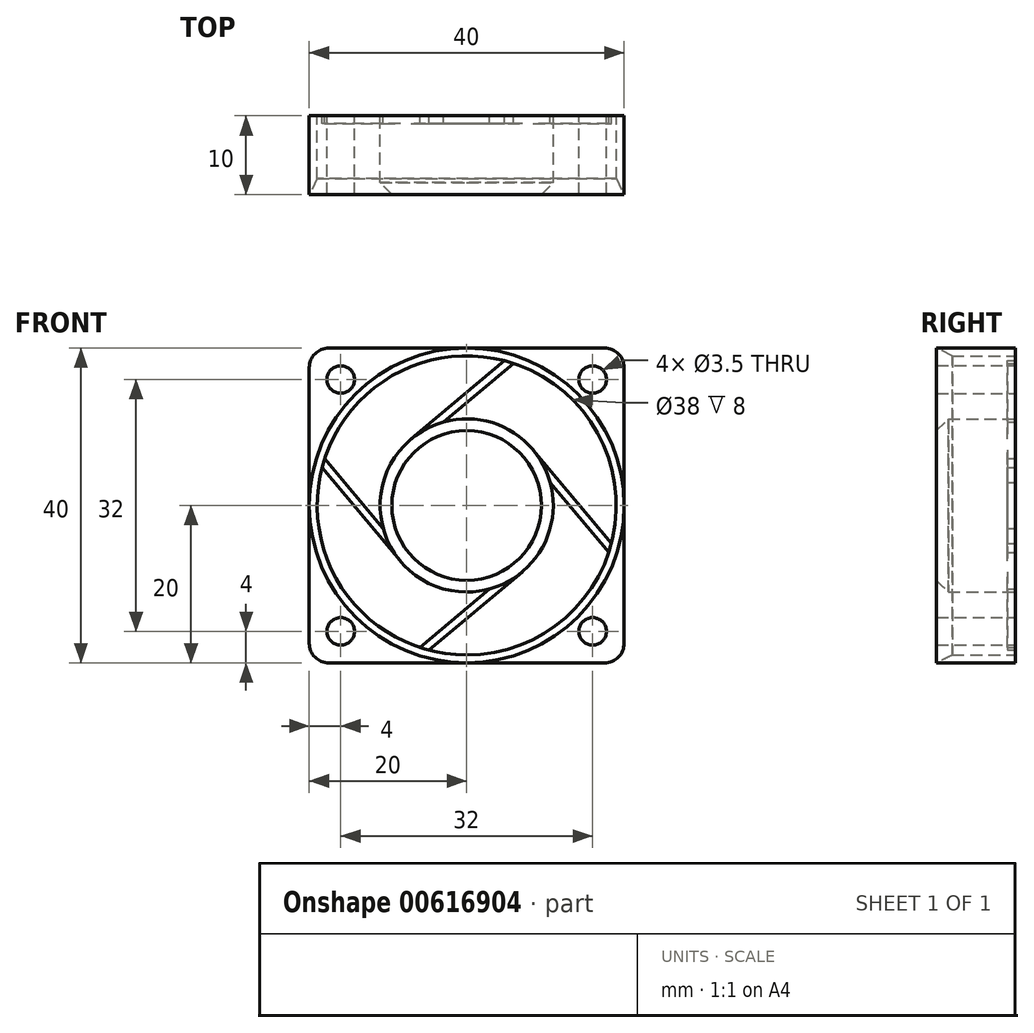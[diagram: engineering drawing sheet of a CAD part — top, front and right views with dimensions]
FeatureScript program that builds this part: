
annotation { "Feature Type Name" : "Feature", "Feature Type Description" : "" }
export const myFeature = defineFeature(function(context is Context, id is Id, definition is map)
    precondition{}
    {
        {
            var Q0;
            Q0=qCreatedBy(makeId("Front.planeOp"),FACE);
            var sketch = newSketch(context, id + "F0", { "sketchPlane" : qUnion([Q0])});
            skLineSegment(sketch, "E0.bottom", {"start": v(17.5, -20) * mm, "end": v(-17.5, -20) * mm});
            skLineSegment(sketch, "E0.top", {"start": v(17.5, 20) * mm, "end": v(-17.5, 20) * mm});
            skLineSegment(sketch, "E0.left", {"start": v(20, -17.5) * mm, "end": v(20, 17.5) * mm});
            skLineSegment(sketch, "E0.right", {"start": v(-20, -17.5) * mm, "end": v(-20, 17.5) * mm});
            skPoint(sketch, "E0.middle", {"position": v(0, 0) * mm});
            skLineSegment(sketch, "E1.bottom", {"start": v(16, 16) * mm, "end": v(-16, 16) * mm, "construction": true});
            skLineSegment(sketch, "E1.top", {"start": v(16, -16) * mm, "end": v(-16, -16) * mm, "construction": true});
            skLineSegment(sketch, "E1.left", {"start": v(16, 16) * mm, "end": v(16, -16) * mm, "construction": true});
            skLineSegment(sketch, "E1.right", {"start": v(-16, 16) * mm, "end": v(-16, -16) * mm, "construction": true});
            skCircle(sketch, "E2", {"center": v(16, 16) * mm, "radius": 1.75 * mm});
            skCircle(sketch, "E3", {"center": v(-16, 16) * mm, "radius": 1.75 * mm});
            skCircle(sketch, "E4", {"center": v(-16, -16) * mm, "radius": 1.75 * mm});
            skCircle(sketch, "E5", {"center": v(16, -16) * mm, "radius": 1.75 * mm});
            skCircle(sketch, "E6", {"center": v(0, 0) * mm, "radius": 19 * mm});
            skPoint(sketch, "E7.visualSharp", {"position": v(20, 20) * mm});
            skArc(sketch, "E7.filletArc", {"start": v(20, 17.5) * mm, "mid": v(19.27, 19.27) * mm, "end": v(17.5, 20) * mm});
            skPoint(sketch, "E8.visualSharp", {"position": v(20, -20) * mm});
            skArc(sketch, "E8.filletArc", {"start": v(17.5, -20) * mm, "mid": v(19.27, -19.27) * mm, "end": v(20, -17.5) * mm});
            skPoint(sketch, "E9.visualSharp", {"position": v(-20, -20) * mm});
            skArc(sketch, "E9.filletArc", {"start": v(-20, -17.5) * mm, "mid": v(-19.27, -19.27) * mm, "end": v(-17.5, -20) * mm});
            skPoint(sketch, "E10.visualSharp", {"position": v(-20, 20) * mm});
            skArc(sketch, "E10.filletArc", {"start": v(-17.5, 20) * mm, "mid": v(-19.27, 19.27) * mm, "end": v(-20, 17.5) * mm});
            skSolve(sketch);
        }
        {
            var Q0;
            Q0 = qSketchRegion(id + "F0", true);
            extrude(context, id + "F1", {"entities" : qUnion([Q0]), "depth" : 10 * mm, "offsetDistance" : 25 * mm});
        }
        {
            var Q0;
            Q0=qCreatedBy(makeId("Front.planeOp"),FACE);
            var sketch = newSketch(context, id + "F2", { "sketchPlane" : qUnion([Q0])});
            skArc(sketch, "E11", {"start": v(-7.07, 8.43) * mm, "mid": v(-10.5, 3.27) * mm, "end": v(-10.6, -2.92) * mm});
            skLineSegment(sketch, "E12", {"start": v(-7.07, 8.43) * mm, "end": v(5.63, 19.09) * mm});
            skLineSegment(sketch, "E13", {"start": v(5.63, 19.09) * mm, "end": v(6.28, 18.32) * mm});
            skLineSegment(sketch, "E14", {"start": v(6.28, 18.32) * mm, "end": v(-2.92, 10.6) * mm});
            skLineSegment(sketch, "E15", {"start": v(0, 0) * mm, "end": v(0, 20) * mm, "construction": true});
            skLineSegment(sketch, "E16.1.0", {"start": v(-18.32, 6.28) * mm, "end": v(-10.6, -2.92) * mm});
            skLineSegment(sketch, "E16.1.1", {"start": v(-8.43, -7.07) * mm, "end": v(-19.09, 5.63) * mm});
            skLineSegment(sketch, "E16.1.2", {"start": v(-19.09, 5.63) * mm, "end": v(-18.32, 6.28) * mm});
            skLineSegment(sketch, "E16.2.0", {"start": v(-6.28, -18.32) * mm, "end": v(2.92, -10.6) * mm});
            skLineSegment(sketch, "E16.2.1", {"start": v(7.07, -8.43) * mm, "end": v(-5.63, -19.09) * mm});
            skLineSegment(sketch, "E16.2.2", {"start": v(-5.63, -19.09) * mm, "end": v(-6.28, -18.32) * mm});
            skLineSegment(sketch, "E16.3.0", {"start": v(18.32, -6.28) * mm, "end": v(10.6, 2.92) * mm});
            skLineSegment(sketch, "E16.3.1", {"start": v(8.43, 7.07) * mm, "end": v(19.09, -5.63) * mm});
            skLineSegment(sketch, "E16.3.2", {"start": v(19.09, -5.63) * mm, "end": v(18.32, -6.28) * mm});
            skArc(sketch, "E17.trimOffspring", {"start": v(8.43, 7.07) * mm, "mid": v(3.27, 10.5) * mm, "end": v(-2.92, 10.6) * mm});
            skArc(sketch, "E18.trimOffspring", {"start": v(7.07, -8.43) * mm, "mid": v(10.5, -3.27) * mm, "end": v(10.6, 2.92) * mm});
            skArc(sketch, "E19.trimOffspring", {"start": v(-8.43, -7.07) * mm, "mid": v(-3.27, -10.5) * mm, "end": v(2.92, -10.6) * mm});
            skSolve(sketch);
        }
        {
            var Q0;
            Q0 = qSketchRegion(id + "F2", true);
            extrude(context, id + "F3", {"entities" : qUnion([Q0]), "operationType" : NewBodyOperationType.ADD, "depth" : 1 * mm, "offsetDistance" : 25 * mm});
        }
        {
            var Q0;
            Q0=makeQuery(id+"F3.opExtrude","CAP_FACE",FACE,{"disambiguationData":[OSD([sQuery(id+"F2.wireOp",EDGE,"E11"),sQuery(id+"F2.wireOp",EDGE,"E12"),sQuery(id+"F2.wireOp",EDGE,"E13"),sQuery(id+"F2.wireOp",EDGE,"E14"),sQuery(id+"F2.wireOp",EDGE,"E16.1.0"),sQuery(id+"F2.wireOp",EDGE,"E16.1.1"),sQuery(id+"F2.wireOp",EDGE,"E16.1.2"),sQuery(id+"F2.wireOp",EDGE,"E16.2.0"),sQuery(id+"F2.wireOp",EDGE,"E16.2.1"),sQuery(id+"F2.wireOp",EDGE,"E16.2.2"),sQuery(id+"F2.wireOp",EDGE,"E16.3.0"),sQuery(id+"F2.wireOp",EDGE,"E16.3.1"),sQuery(id+"F2.wireOp",EDGE,"E16.3.2"),sQuery(id+"F2.wireOp",EDGE,"E17.trimOffspring"),sQuery(id+"F2.wireOp",EDGE,"E18.trimOffspring"),sQuery(id+"F2.wireOp",EDGE,"E19.trimOffspring")])],"isStart":false});
            var sketch = newSketch(context, id + "F4", { "sketchPlane" : qUnion([Q0])});
            skCircle(sketch, "E20", {"center": v(0, 0) * mm, "radius": 11 * mm});
            skSolve(sketch);
        }
        {
            var Q0;
            Q0 = qSketchRegion(id + "F4", true);
            extrude(context, id + "F5", {"entities" : qUnion([Q0]), "operationType" : NewBodyOperationType.ADD, "depth" : 9 * mm, "offsetDistance" : 25 * mm});
        }
        {
            var Q0;
            Q0=makeQuery(id+"F5.opExtrude","CAP_EDGE",EDGE,{"disambiguationData":[OSD([sQuery(id+"F4.wireOp",EDGE,"E20")])],"isStart":false});
            chamfer(context, id + "F6", {"entities" : qUnion([Q0]), "width" : 1.5 * mm, "tangentPropagation" : true});
        }
        {
            var Q0;
            Q0=makeQuery(id+"F1.opExtrude","CAP_EDGE",EDGE,{"disambiguationData":[OSD([sQuery(id+"F0.wireOp",EDGE,"E6")])],"isStart":false});
            chamfer(context, id + "F7", {"entities" : qUnion([Q0]), "chamferType" : ChamferType.TWO_OFFSETS, "width1" : 2 * mm, "oppositeDirection" : false, "width2" : 1 * mm, "tangentPropagation" : true});
        }
    });
